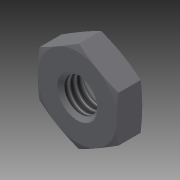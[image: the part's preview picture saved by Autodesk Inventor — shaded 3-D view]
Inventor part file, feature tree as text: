
AUTODESK INVENTOR PART (.ipt)
format: ipt  version: 2014 (Build 180170000, 170)  size: 157,696 bytes
history: native  units: in
note: dims shown in document units (in); Inventor stores cm internally (conversion verified against a paired STEP export)
features: other x70, sketch x3, revolve x2, extrude x1, thread x1
ambient origin geometry x8: Origin, YZ Plane, XZ Plane, XY Plane, X Axis, Y Axis, Z Axis, Center Point
bodies: Solid1 (feature_tree)
feature tree (77):
  sketch  "Sketch_8"  dims[d0=360.0deg d1=0.12in d2=0.0in]
  sketch  "Sketch_10"  dims[d3=360.0deg d4=0.0862in d5=0.0in]
  revolve  "Revolution1"  [1 undecoded]
  extrude  "Extrusion1"  Depth=0.0862in TaperAngle=0.0deg
  revolve  "Revolution2"  [1 undecoded]
  thread  "Thread1"  [1 undecoded]
  other  "NUT_XY"
  other  "NUT_YZ"
  other  "NUT_ZX"
  other  "NUT_X"
  other  "NUT_Y"
  other  "NUT_Z"
  other  "NUT_Center"
  other  "a1_XY"
  other  "a1_YZ"
  other  "a1_ZX"
  other  "a1_X"
  other  "a1_Y"
  other  "a1_Z"
  other  "a1_Center"
  other  "a2_XY"
  other  "a2_YZ"
  other  "a2_ZX"
  other  "a2_X"
  other  "a2_Y"
  other  "a2_Z"
  other  "a2_Center"
  other  "b1_XY"
  other  "b1_YZ"
  other  "b1_ZX"
  other  "b1_X"
  other  "b1_Y"
  other  "b1_Z"
  other  "b1_Center"
  other  "b2_XY"
  other  "b2_YZ"
  other  "b2_ZX"
  other  "b2_X"
  other  "b2_Y"
  other  "b2_Z"
  other  "b2_Center"
  other  "e_XY"
  other  "e_YZ"
  other  "e_ZX"
  other  "e_X"
  other  "e_Y"
  other  "e_Z"
  other  "e_Center"
  other  "ol1_XY"
  other  "ol1_YZ"
  other  "ol1_ZX"
  other  "ol1_X"
  other  "ol1_Y"
  other  "ol1_Z"
  other  "ol1_Center"
  other  "ol2_XY"
  other  "ol2_YZ"
  other  "ol2_ZX"
  other  "ol2_X"
  other  "ol2_Y"
  other  "ol2_Z"
  other  "ol2_Center"
  other  "th1_XY"
  other  "th1_YZ"
  other  "th1_ZX"
  other  "th1_X"
  other  "th1_Y"
  other  "th1_Z"
  other  "th1_Center"
  other  "th2_XY"
  other  "th2_YZ"
  other  "th2_ZX"
  other  "th2_X"
  other  "th2_Y"
  other  "th2_Z"
  other  "th2_Center"
  sketch  "Sketch_11"
note: 3 required parameter values undecoded (feature->parameter linkage not recoverable at this tier; creation-order binding heuristic only, values carry confidence <= 0.55)